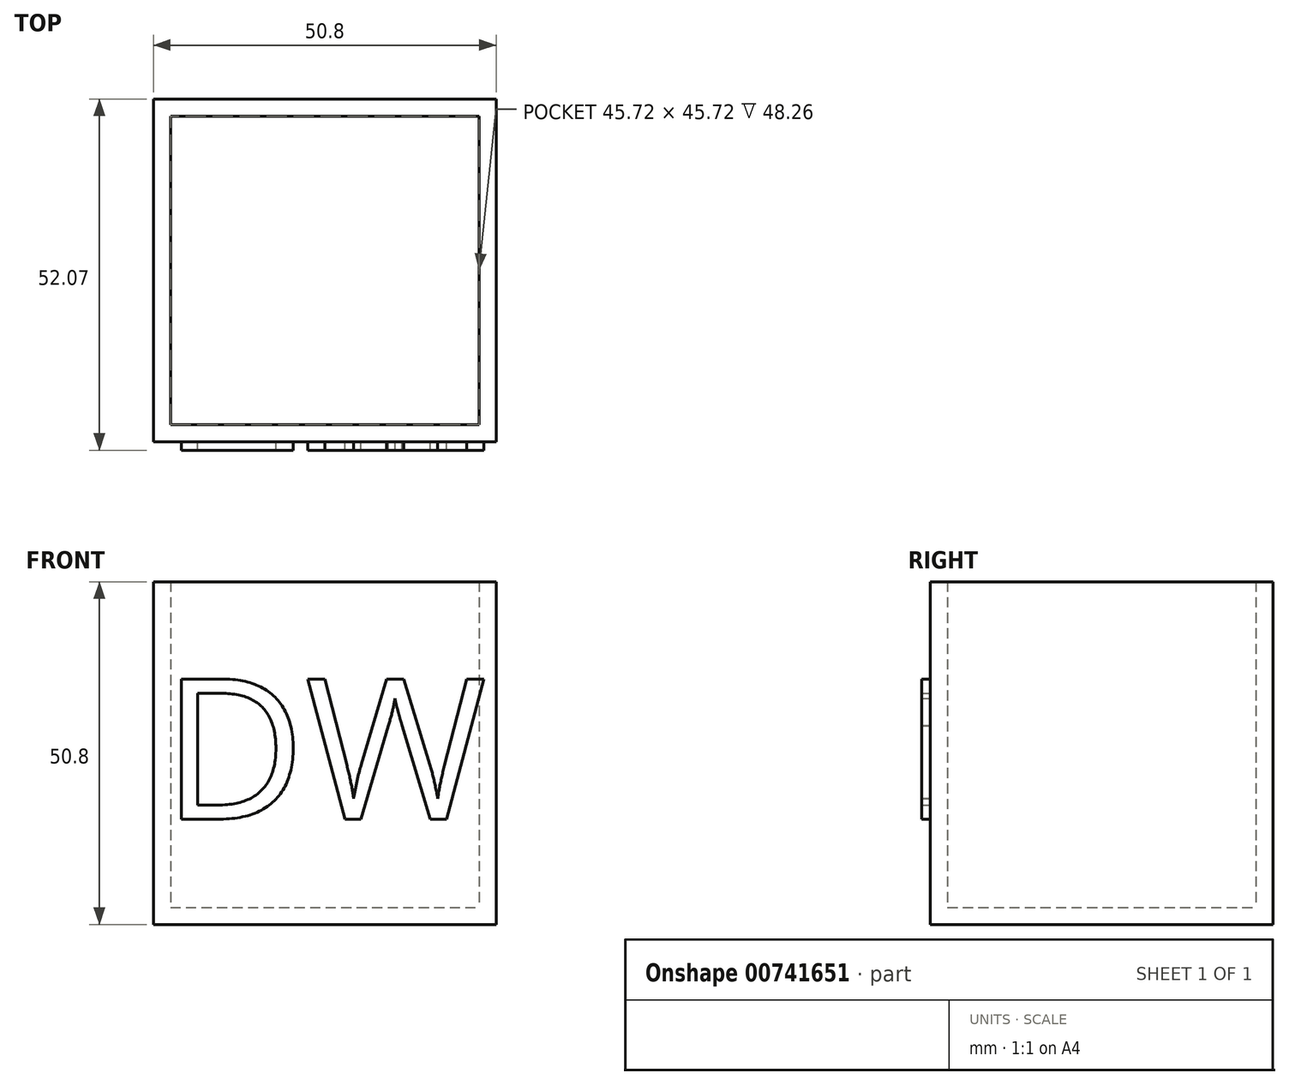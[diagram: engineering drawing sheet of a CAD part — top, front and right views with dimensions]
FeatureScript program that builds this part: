
annotation { "Feature Type Name" : "Feature", "Feature Type Description" : "" }
export const myFeature = defineFeature(function(context is Context, id is Id, definition is map)
    precondition{}
    {
        {
            var Q0;
            Q0=qCreatedBy(makeId("Front.planeOp"),FACE);
            var sketch = newSketch(context, id + "F0", { "sketchPlane" : qUnion([Q0])});
            skLineSegment(sketch, "E0.bottom", {"start": v(-71.68, 77.52) * mm, "end": v(-20.88, 77.52) * mm});
            skLineSegment(sketch, "E0.top", {"start": v(-71.68, 26.72) * mm, "end": v(-20.88, 26.72) * mm});
            skLineSegment(sketch, "E0.left", {"start": v(-71.68, 77.52) * mm, "end": v(-71.68, 26.72) * mm});
            skLineSegment(sketch, "E0.right", {"start": v(-20.88, 77.52) * mm, "end": v(-20.88, 26.72) * mm});
            skSolve(sketch);
        }
        {
            var Q0;
            Q0=makeQuery(id+"F0.imprint","IMPRINT",FACE,{"disambiguationData":[TD([[makeQuery(id+"F0.imprint","IMPRINT",EDGE,{"derivedFrom":sQuery(id+"F0.wireOp",EDGE,"E0.bottom")}),-1.0]])]});
            extrude(context, id + "F1", {"entities" : qUnion([Q0]), "depth" : 50.8 * mm, "offsetDistance" : 25.4 * mm});
        }
        {
            var Q0;
            Q0=makeQuery(id+"F1.opExtrude","SWEPT_FACE",FACE,{"disambiguationData":[OSD([sQuery(id+"F0.wireOp",EDGE,"E0.bottom")])]});
            shell(context, id + "F2", {"entities" : qUnion([Q0]), "thickness" : 2.54 * mm});
        }
        {
            var Q0;
            Q0=makeQuery(id+"F1.opExtrude","CAP_FACE",FACE,{"disambiguationData":[OSD([sQuery(id+"F0.wireOp",EDGE,"E0.bottom"),sQuery(id+"F0.wireOp",EDGE,"E0.top"),sQuery(id+"F0.wireOp",EDGE,"E0.left"),sQuery(id+"F0.wireOp",EDGE,"E0.right")])],"isStart":false});
            var sketch = newSketch(context, id + "F3", { "sketchPlane" : qUnion([Q0])});
            skText(sketch, "E1", { "text": "DW", "fontName": "OpenSans-Regular.ttf"});
            const initialGuessF3  = {"E1": [-0.07036, 0.04234, 1, 0, 0.02091]};
            skSetInitialGuess(sketch, initialGuessF3);
            skSolve(sketch);
        }
        {
            var Q0;
            Q0 = qSketchRegion(id + "F3", true);
            extrude(context, id + "F4", {"entities" : qUnion([Q0]), "operationType" : NewBodyOperationType.ADD, "depth" : 1.27 * mm, "offsetDistance" : 25.4 * mm});
        }
    });
